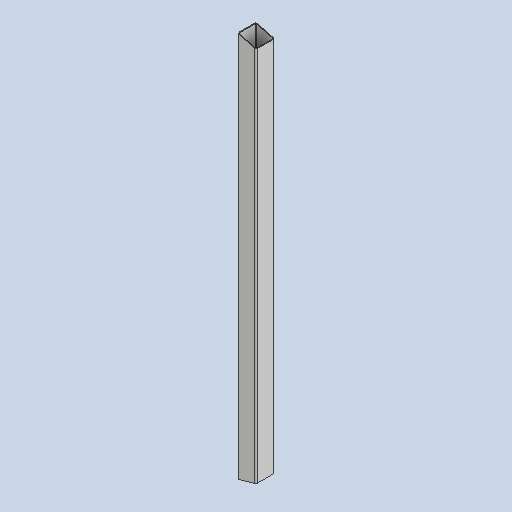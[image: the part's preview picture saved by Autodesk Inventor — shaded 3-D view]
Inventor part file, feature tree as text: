
AUTODESK INVENTOR PART (.ipt)
format: ipt  version: 2025 (Build 290162010, 162A)  size: 181,760 bytes
history: native  units: mm
features: extrude x2, sketch x2, mirror x1
ambient origin geometry x8: Origin, YZ Plane, XZ Plane, XY Plane, X Axis, Y Axis, Z Axis, Center Point
bodies: Solid1 (feature_tree)
feature tree (5):
  extrude  "Extrusion1"  Depth=8.0mm
  extrude  "Extrusion2"  Depth=120.0mm
  mirror  "Mirror1"
  sketch  "Sketch1"  dims[d0=8.0mm d1=120.0mm d2=120.0mm d3=4.0mm d6=8.0mm]
  sketch  "Sketch2"  dims[d7=120.0mm d8=120.0mm d9=4.0mm d14=2506.306mm d15=0.0mm d16=15.0deg d17=2000.0mm d18=0.0mm]
